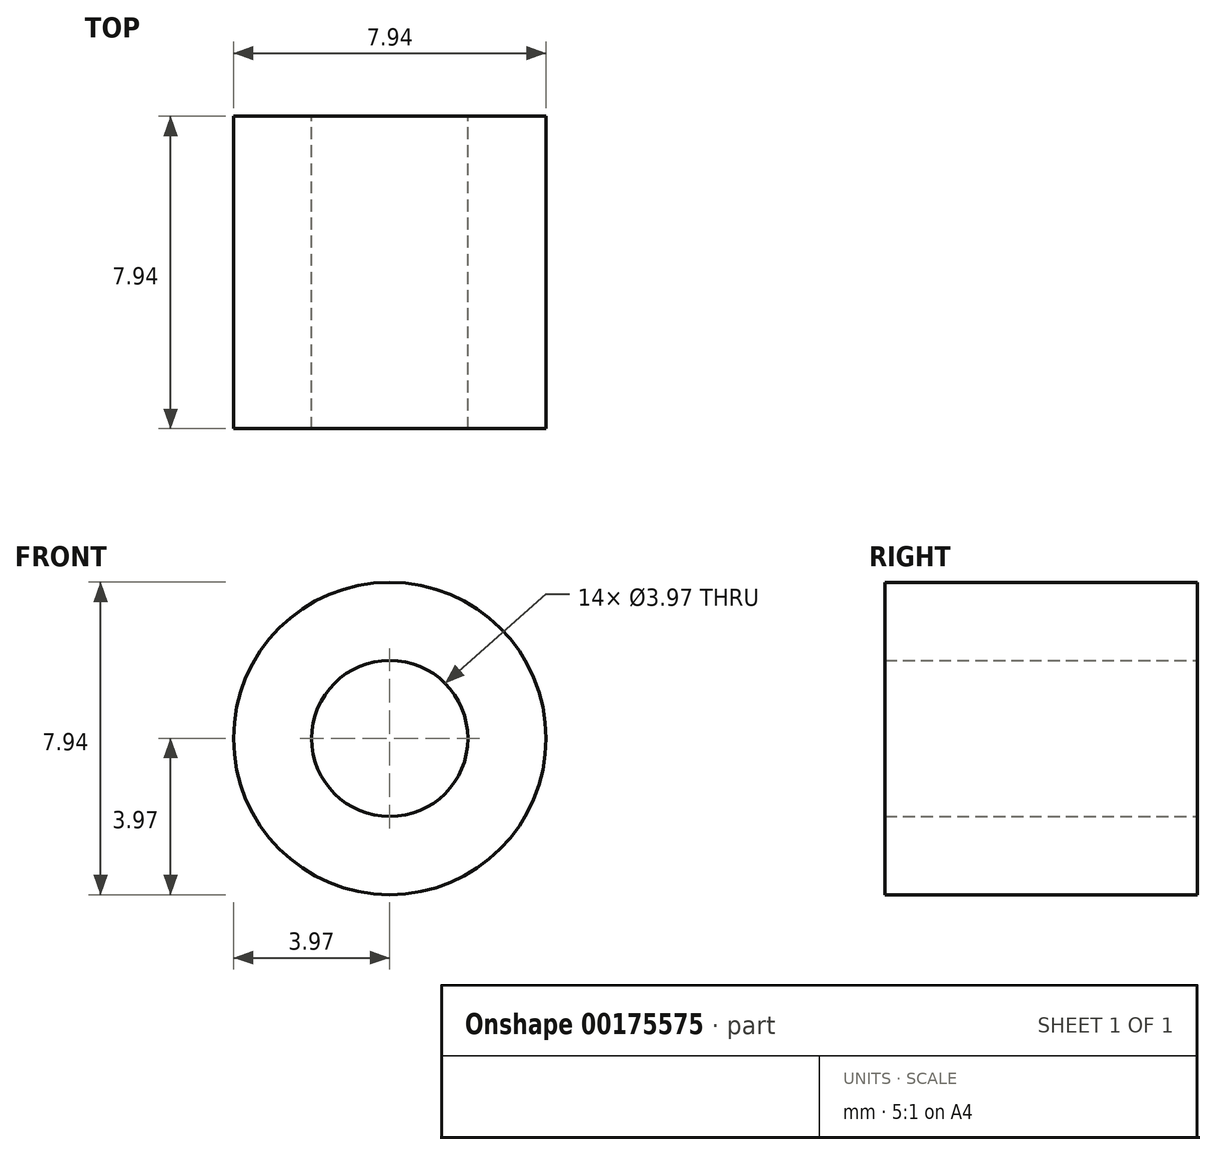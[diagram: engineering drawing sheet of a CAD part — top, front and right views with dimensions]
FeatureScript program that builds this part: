
annotation { "Feature Type Name" : "Feature", "Feature Type Description" : "" }
export const myFeature = defineFeature(function(context is Context, id is Id, definition is map)
    precondition{}
    {
        {
            var Q0;
            Q0=qCreatedBy(makeId("Front.planeOp"),FACE);
            var sketch = newSketch(context, id + "F0", { "sketchPlane" : qUnion([Q0])});
            skCircle(sketch, "E0", {"center": v(0, 0) * mm, "radius": 1.98 * mm});
            skCircle(sketch, "E1", {"center": v(0, 0) * mm, "radius": 3.97 * mm});
            skSolve(sketch);
        }
        {
            var Q0;
            Q0=makeQuery(id+"F0.imprint","IMPRINT",FACE,{"disambiguationData":[TD([[makeQuery(id+"F0.imprint","IMPRINT",EDGE,{"derivedFrom":sQuery(id+"F0.wireOp",EDGE,"E0")}),-1.0]])]});
            extrude(context, id + "F1", {"entities" : qUnion([Q0]), "endBound" : BoundingType.SYMMETRIC, "depth" : 7.94 * mm});
        }
    });
